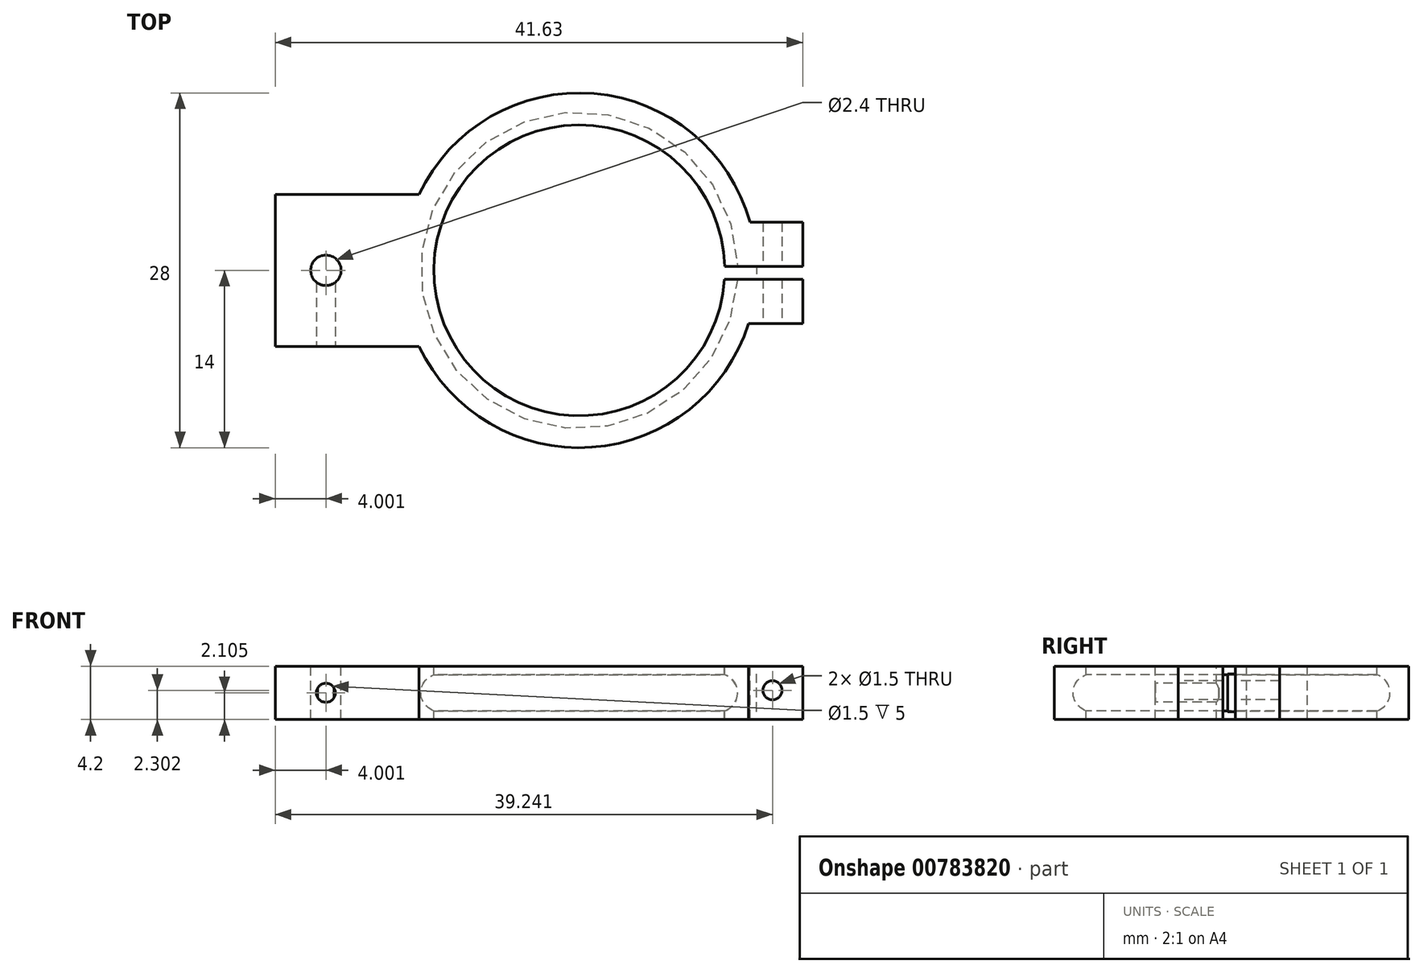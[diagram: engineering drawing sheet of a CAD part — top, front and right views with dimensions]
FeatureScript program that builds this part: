
annotation { "Feature Type Name" : "Feature", "Feature Type Description" : "" }
export const myFeature = defineFeature(function(context is Context, id is Id, definition is map)
    precondition{}
    {
        {
            var Q0;
            Q0=qCreatedBy(makeId("Front.planeOp"),FACE);
            var sketch = newSketch(context, id + "F0", { "sketchPlane" : qUnion([Q0])});
            skLineSegment(sketch, "E0", {"start": v(-17.32, 27.47) * mm, "end": v(-17.32, -17.12) * mm});
            skCircle(sketch, "E1", {"center": v(-28.32, 5.45) * mm, "radius": 1.5 * mm});
            skLineSegment(sketch, "E2", {"start": v(-28.32, 8.17) * mm, "end": v(-28.32, 2.71) * mm});
            skLineSegment(sketch, "E3", {"start": v(-28.32, 6.95) * mm, "end": v(-31.32, 6.95) * mm});
            skLineSegment(sketch, "E4", {"start": v(-28.32, 3.95) * mm, "end": v(-31.32, 3.95) * mm});
            skLineSegment(sketch, "E5", {"start": v(-31.32, 3.95) * mm, "end": v(-31.32, 6.95) * mm});
            skPoint(sketch, "E6.end.orphan", {"position": v(-28.32, 4.15) * mm});
            skPoint(sketch, "E6.start.orphan", {"position": v(-28.32, 6.75) * mm});
            skSolve(sketch);
        }
        {
            var Q0;
            {var subQ0=sQuery(id+"F0.wireOp",EDGE,"E3");Q0=makeQuery(id+"F0.imprint","IMPRINT",FACE,{"disambiguationData":[TD([[makeQuery(id+"F0.imprint","IMPRINT",EDGE,{"derivedFrom":subQ0}),1.0]])]});}
            var Q1;
            {var subQ0=sQuery(id+"F0.wireOp",EDGE,"4f6HL5Te-FB6r-DQlG-h35e-if1vYiqSxlt2");Q1=makeQuery(id+"F0.imprint","IMPRINT",FACE,{"disambiguationData":[TD([[makeQuery(id+"F0.imprint","IMPRINT",EDGE,{"derivedFrom":subQ0}),-1.0]])]});}
            var Q2;
            Q2=sQuery(id+"F0.wireOp",EDGE,"E0");
            revolve(context, id + "F1", {"surfaceOperationType" : NewSurfaceOperationType.NEW, "entities" : qUnion([Q0, Q1]), "axis" : qUnion([Q2]), "revolveType" : RevolveType.FULL});
        }
        {
            var Q0;
            Q0=makeQuery(id+"F1.opRevolve","SWEPT_FACE",FACE,{"disambiguationData":[OSD([sQuery(id+"F0.wireOp",EDGE,"E3")])]});
            var sketch = newSketch(context, id + "F2", { "sketchPlane" : qUnion([Q0])});
            skLineSegment(sketch, "E7.bottom", {"start": v(-4.13, 0.3) * mm, "end": v(-0.19, 0.3) * mm});
            skLineSegment(sketch, "E7.top", {"start": v(-4.13, 3.8) * mm, "end": v(-0.19, 3.8) * mm});
            skLineSegment(sketch, "E7.left", {"start": v(-4.13, 0.3) * mm, "end": v(-4.13, 3.8) * mm});
            skLineSegment(sketch, "E7.right", {"start": v(-0.19, 0.3) * mm, "end": v(-0.19, 3.8) * mm});
            skLineSegment(sketch, "E8.bottom", {"start": v(-4.13, -0.7) * mm, "end": v(-0.19, -0.7) * mm});
            skLineSegment(sketch, "E8.top", {"start": v(-4.13, -4.2) * mm, "end": v(-0.19, -4.2) * mm});
            skLineSegment(sketch, "E8.left", {"start": v(-4.13, -0.7) * mm, "end": v(-4.13, -4.2) * mm});
            skLineSegment(sketch, "E8.right", {"start": v(-0.19, -0.7) * mm, "end": v(-0.19, -4.2) * mm});
            skLineSegment(sketch, "E9.bottom", {"start": v(-29.4, 6) * mm, "end": v(-41.32, 6) * mm});
            skLineSegment(sketch, "E9.top", {"start": v(-29.4, -6) * mm, "end": v(-41.32, -6) * mm});
            skLineSegment(sketch, "E9.left", {"start": v(-29.4, 6) * mm, "end": v(-29.4, -6) * mm});
            skLineSegment(sketch, "E9.right", {"start": v(-41.32, 6) * mm, "end": v(-41.32, -6) * mm});
            skCircle(sketch, "E10", {"center": v(-37.32, 0) * mm, "radius": 1.2 * mm});
            skPoint(sketch, "E11", {"position": v(-17.32, 0) * mm});
            skSolve(sketch);
        }
        {
            var Q0;
            {var subQ0=sQuery(id+"F2.wireOp",EDGE,"E9.right");Q0=makeQuery(id+"F2.imprint","IMPRINT",FACE,{"disambiguationData":[TD([[makeQuery(id+"F2.imprint","IMPRINT",EDGE,{"derivedFrom":subQ0}),1.0]])]});}
            var Q1;
            {var subQ0=sQuery(id+"F2.wireOp",EDGE,"E7.right");Q1=makeQuery(id+"F2.imprint","IMPRINT",FACE,{"disambiguationData":[TD([[makeQuery(id+"F2.imprint","IMPRINT",EDGE,{"derivedFrom":subQ0}),1.0]])]});}
            var Q2;
            {var subQ0=sQuery(id+"F2.wireOp",EDGE,"E8.right");Q2=makeQuery(id+"F2.imprint","IMPRINT",FACE,{"disambiguationData":[TD([[makeQuery(id+"F2.imprint","IMPRINT",EDGE,{"derivedFrom":subQ0}),-1.0]])]});}
            extrude(context, id + "F3", {"entities" : qUnion([Q0, Q1, Q2]), "operationType" : NewBodyOperationType.ADD, "oppositeDirection" : true, "depth" : 3 * mm, "offsetDistance" : 25 * mm});
        }
        {
            var Q0;
            {var subQ0=sQuery(id+"F0.wireOp",EDGE,"E5");var subQ1=sQuery(id+"F0.wireOp",EDGE,"E3");Q0=makeQuery(id+"F3.boolean.opBoolean","MERGE",FACE,{"derivedFrom":[makeQuery(id+"F1.opRevolve","SWEPT_FACE",FACE,{"disambiguationData":[OSD([subQ1])]}),makeQuery(id+"F3.opExtrude","CAP_FACE",FACE,{"disambiguationData":[OSD([subQ1,subQ0,sQuery(id+"F2.wireOp",EDGE,"E7.bottom"),sQuery(id+"F2.wireOp",EDGE,"E7.top"),sQuery(id+"F2.wireOp",EDGE,"E7.right")])],"isStart":true}),makeQuery(id+"F3.opExtrude","CAP_FACE",FACE,{"disambiguationData":[OSD([subQ1,subQ0,sQuery(id+"F2.wireOp",EDGE,"E8.bottom"),sQuery(id+"F2.wireOp",EDGE,"E8.top"),sQuery(id+"F2.wireOp",EDGE,"E8.right")])],"isStart":true}),makeQuery(id+"F3.opExtrude","CAP_FACE",FACE,{"disambiguationData":[OSD([subQ1,subQ0,sQuery(id+"F2.wireOp",EDGE,"E9.bottom"),sQuery(id+"F2.wireOp",EDGE,"E9.top"),sQuery(id+"F2.wireOp",EDGE,"E9.right"),sQuery(id+"F2.wireOp",EDGE,"E10")])],"isStart":true})]});}
            var sketch = newSketch(context, id + "F4", { "sketchPlane" : qUnion([Q0])});
            skLineSegment(sketch, "E12.bottom", {"start": v(-3.32, 0.3) * mm, "end": v(-6.95, 0.3) * mm});
            skLineSegment(sketch, "E12.top", {"start": v(-3.32, -0.7) * mm, "end": v(-6.95, -0.7) * mm});
            skLineSegment(sketch, "E12.left", {"start": v(-3.32, 0.3) * mm, "end": v(-3.32, -0.7) * mm});
            skLineSegment(sketch, "E12.right", {"start": v(-6.95, 0.3) * mm, "end": v(-6.95, -0.7) * mm});
            skSolve(sketch);
        }
        {
            var Q0;
            {var subQ3=sQuery(id+"F0.wireOp",EDGE,"E3");var subQ9=makeQuery(id+"F1.opRevolve","SWEPT_EDGE",EDGE,{"disambiguationData":[OSD([sQuery(id+"F0.wireOp",EDGE,"E1"),sQuery(id+"F0.wireOp",EDGE,"E2"),sQuery(id+"F0.wireOp",EDGE,"4f6HL5Te-FB6r-DQlG-h35e-if1vYiqSxlt2"),subQ3])]});var subQ11=sQuery(id+"F4.wireOp",EDGE,"E12.bottom");var subQ13=makeQuery(id+"F4.imprint","INTERSECT",VERTEX,{"derivedFrom":[subQ9,subQ11]});Q0=makeQuery(id+"F4.imprint","IMPRINT",FACE,{"disambiguationData":[TD([[makeQuery(id+"F4.imprint","IMPRINT",EDGE,{"disambiguationData":[TD([[subQ13,1.0]])],"derivedFrom":subQ9}),-1.0]])]});}
            var Q1;
            {var subQ0=sQuery(id+"F4.wireOp",EDGE,"E12.right");Q1=makeQuery(id+"F4.imprint","IMPRINT",FACE,{"disambiguationData":[TD([[makeQuery(id+"F4.imprint","IMPRINT",EDGE,{"derivedFrom":subQ0}),1.0]])]});}
            extrude(context, id + "F5", {"entities" : qUnion([Q0, Q1]), "operationType" : NewBodyOperationType.REMOVE, "oppositeDirection" : true, "depth" : 25 * mm, "offsetDistance" : 25 * mm});
        }
        {
            var Q0;
            Q0=makeQuery(id+"F3.opExtrude","SWEPT_FACE",FACE,{"disambiguationData":[OSD([sQuery(id+"F2.wireOp",EDGE,"E8.top")])]});
            var sketch = newSketch(context, id + "F6", { "sketchPlane" : qUnion([Q0])});
            skCircle(sketch, "E13", {"center": v(-2.08, 5.65) * mm, "radius": 0.75 * mm});
            skSolve(sketch);
        }
        {
            var Q0;
            Q0 = qSketchRegion(id + "F6", true);
            extrude(context, id + "F7", {"entities" : qUnion([Q0]), "operationType" : NewBodyOperationType.REMOVE, "oppositeDirection" : true, "depth" : 25 * mm, "offsetDistance" : 25 * mm});
        }
        {
            var Q0;
            Q0=makeQuery(id+"F3.opExtrude","SWEPT_FACE",FACE,{"disambiguationData":[OSD([sQuery(id+"F2.wireOp",EDGE,"E9.top")])]});
            var sketch = newSketch(context, id + "F8", { "sketchPlane" : qUnion([Q0])});
            skCircle(sketch, "E14", {"center": v(-37.32, 5.45) * mm, "radius": 0.75 * mm});
            skPoint(sketch, "E14.centerSnap0", {"position": v(-41.32, 5.45) * mm});
            skSolve(sketch);
        }
        {
            var Q0;
            Q0=makeQuery(id+"F8.imprint","IMPRINT",FACE,{"disambiguationData":[TD([[makeQuery(id+"F8.imprint","IMPRINT",EDGE,{"derivedFrom":sQuery(id+"F8.wireOp",EDGE,"E14")}),1.0]])]});
            extrude(context, id + "F9", {"entities" : qUnion([Q0]), "operationType" : NewBodyOperationType.REMOVE, "oppositeDirection" : true, "depth" : 5 * mm, "offsetDistance" : 25 * mm});
        }
        {
            var Q0;
            {var subQ0=sQuery(id+"F0.wireOp",EDGE,"E5");var subQ1=sQuery(id+"F0.wireOp",EDGE,"E3");Q0=makeQuery(id+"F3.boolean.opBoolean","MERGE",FACE,{"derivedFrom":[makeQuery(id+"F1.opRevolve","SWEPT_FACE",FACE,{"disambiguationData":[OSD([subQ1])]}),makeQuery(id+"F3.opExtrude","CAP_FACE",FACE,{"disambiguationData":[OSD([subQ1,subQ0,sQuery(id+"F2.wireOp",EDGE,"E7.bottom"),sQuery(id+"F2.wireOp",EDGE,"E7.top"),sQuery(id+"F2.wireOp",EDGE,"E7.right")])],"isStart":true}),makeQuery(id+"F3.opExtrude","CAP_FACE",FACE,{"disambiguationData":[OSD([subQ1,subQ0,sQuery(id+"F2.wireOp",EDGE,"E8.bottom"),sQuery(id+"F2.wireOp",EDGE,"E8.top"),sQuery(id+"F2.wireOp",EDGE,"E8.right")])],"isStart":true}),makeQuery(id+"F3.opExtrude","CAP_FACE",FACE,{"disambiguationData":[OSD([subQ1,subQ0,sQuery(id+"F2.wireOp",EDGE,"E9.bottom"),sQuery(id+"F2.wireOp",EDGE,"E9.top"),sQuery(id+"F2.wireOp",EDGE,"E9.right"),sQuery(id+"F2.wireOp",EDGE,"E10")])],"isStart":true})]});}
            var sketch = newSketch(context, id + "F10", { "sketchPlane" : qUnion([Q0])});
            skSolve(sketch);
        }
        {
            var Q0;
            {var subQ7=sQuery(id+"F2.wireOp",EDGE,"E7.top");Q0=makeQuery(id+"F10.imprint","IMPRINT",FACE,{"disambiguationData":[TD([[makeQuery(id+"F10.imprint","IMPRINT",EDGE,{"derivedFrom":makeQuery(id+"F3.opExtrude","CAP_EDGE",EDGE,{"disambiguationData":[OSD([subQ7])],"isStart":true})}),-1.0]])]});}
            extrude(context, id + "F11", {"entities" : qUnion([Q0]), "operationType" : NewBodyOperationType.ADD, "depth" : 0.6 * mm, "offsetDistance" : 25 * mm});
        }
        {
            var Q0;
            {var subQ0=sQuery(id+"F0.wireOp",EDGE,"E5");var subQ1=sQuery(id+"F0.wireOp",EDGE,"E3");Q0=makeQuery(id+"F3.boolean.opBoolean","MERGE",FACE,{"derivedFrom":[makeQuery(id+"F1.opRevolve","SWEPT_FACE",FACE,{"disambiguationData":[OSD([sQuery(id+"F0.wireOp",EDGE,"E4")])]}),makeQuery(id+"F3.opExtrude","CAP_FACE",FACE,{"disambiguationData":[OSD([subQ1,subQ0,sQuery(id+"F2.wireOp",EDGE,"E7.bottom"),sQuery(id+"F2.wireOp",EDGE,"E7.top"),sQuery(id+"F2.wireOp",EDGE,"E7.right")])],"isStart":false}),makeQuery(id+"F3.opExtrude","CAP_FACE",FACE,{"disambiguationData":[OSD([subQ1,subQ0,sQuery(id+"F2.wireOp",EDGE,"E8.bottom"),sQuery(id+"F2.wireOp",EDGE,"E8.top"),sQuery(id+"F2.wireOp",EDGE,"E8.right")])],"isStart":false}),makeQuery(id+"F3.opExtrude","CAP_FACE",FACE,{"disambiguationData":[OSD([subQ1,subQ0,sQuery(id+"F2.wireOp",EDGE,"E9.bottom"),sQuery(id+"F2.wireOp",EDGE,"E9.top"),sQuery(id+"F2.wireOp",EDGE,"E9.right"),sQuery(id+"F2.wireOp",EDGE,"E10")])],"isStart":false})]});}
            var sketch = newSketch(context, id + "F12", { "sketchPlane" : qUnion([Q0])});
            skSolve(sketch);
        }
        {
            var Q0;
            {var subQ6=sQuery(id+"F2.wireOp",EDGE,"E7.top");Q0=makeQuery(id+"F12.imprint","IMPRINT",FACE,{"disambiguationData":[TD([[makeQuery(id+"F12.imprint","IMPRINT",EDGE,{"derivedFrom":makeQuery(id+"F3.opExtrude","CAP_EDGE",EDGE,{"disambiguationData":[OSD([subQ6])],"isStart":false})}),1.0]])]});}
            extrude(context, id + "F13", {"entities" : qUnion([Q0]), "operationType" : NewBodyOperationType.ADD, "depth" : 0.6 * mm, "offsetDistance" : 25 * mm});
        }
        {
            var Q0;
            {var subQ0=sQuery(id+"F2.wireOp",EDGE,"E7.right");Q0=makeQuery(id+"F13.boolean.opBoolean","MERGE",FACE,{"derivedFrom":[makeQuery(id+"F11.boolean.opBoolean","MERGE",FACE,{"derivedFrom":[makeQuery(id+"F3.opExtrude","SWEPT_FACE",FACE,{"disambiguationData":[OSD([subQ0])]}),makeQuery(id+"F11.opExtrude","SWEPT_FACE",FACE,{"disambiguationData":[OSD([subQ0])]})]}),makeQuery(id+"F13.opExtrude","SWEPT_FACE",FACE,{"disambiguationData":[OSD([subQ0])]})]});}
            var sketch = newSketch(context, id + "F14", { "sketchPlane" : qUnion([Q0])});
            skSolve(sketch);
        }
        {
            var Q0;
            {var subQ0=sQuery(id+"F2.wireOp",EDGE,"E7.right");Q0=makeQuery(id+"F14.imprint","IMPRINT",FACE,{"disambiguationData":[TD([[makeQuery(id+"F14.imprint","IMPRINT",EDGE,{"derivedFrom":makeQuery(id+"F11.opExtrude","CAP_EDGE",EDGE,{"disambiguationData":[OSD([subQ0])],"isStart":false})}),-1.0]])]});}
            var Q1;
            {var subQ0=sQuery(id+"F2.wireOp",EDGE,"E8.right");Q1=makeQuery(id+"F13.boolean.opBoolean","MERGE",FACE,{"derivedFrom":[makeQuery(id+"F11.boolean.opBoolean","MERGE",FACE,{"derivedFrom":[makeQuery(id+"F3.opExtrude","SWEPT_FACE",FACE,{"disambiguationData":[OSD([subQ0])]}),makeQuery(id+"F11.opExtrude","SWEPT_FACE",FACE,{"disambiguationData":[OSD([subQ0])]})]}),makeQuery(id+"F13.opExtrude","SWEPT_FACE",FACE,{"disambiguationData":[OSD([subQ0])]})]});}
            extrude(context, id + "F15", {"entities" : qUnion([Q0, Q1]), "operationType" : NewBodyOperationType.ADD, "depth" : 0.5 * mm, "offsetDistance" : 25 * mm});
        }
        {
            var Q0;
            {var subQ0=sQuery(id+"F2.wireOp",EDGE,"E7.right");var subQ1=sQuery(id+"F2.wireOp",EDGE,"E8.right");Q0=makeQuery(id+"F15.boolean.opBoolean","MERGE",FACE,{"derivedFrom":[makeQuery(id+"F11.opExtrude","CAP_FACE",FACE,{"disambiguationData":[OSD([sQuery(id+"F0.wireOp",EDGE,"E1"),sQuery(id+"F0.wireOp",EDGE,"E2"),sQuery(id+"F0.wireOp",EDGE,"E3"),sQuery(id+"F0.wireOp",EDGE,"E5"),sQuery(id+"F2.wireOp",EDGE,"E7.bottom"),sQuery(id+"F2.wireOp",EDGE,"E7.top"),subQ0,sQuery(id+"F2.wireOp",EDGE,"E8.bottom"),sQuery(id+"F2.wireOp",EDGE,"E8.top"),subQ1,sQuery(id+"F2.wireOp",EDGE,"E9.bottom"),sQuery(id+"F2.wireOp",EDGE,"E9.top"),sQuery(id+"F2.wireOp",EDGE,"E9.right"),sQuery(id+"F2.wireOp",EDGE,"E10"),sQuery(id+"F4.wireOp",EDGE,"E12.bottom"),sQuery(id+"F4.wireOp",EDGE,"E12.top")])],"isStart":false}),makeQuery(id+"F15.opExtrude","SWEPT_FACE",FACE,{"disambiguationData":[OSD([subQ1]),TDD([makeQuery(id+"F11.opExtrude","CAP_EDGE",EDGE,{"disambiguationData":[OSD([subQ1])],"isStart":false})])]}),makeQuery(id+"F15.opExtrude","SWEPT_FACE",FACE,{"disambiguationData":[OSD([subQ0]),TDD([makeQuery(id+"F14.imprint","IMPRINT",EDGE,{"derivedFrom":makeQuery(id+"F11.opExtrude","CAP_EDGE",EDGE,{"disambiguationData":[OSD([subQ0])],"isStart":false})})])]})]});}
            var sketch = newSketch(context, id + "F16", { "sketchPlane" : qUnion([Q0])});
            skCircle(sketch, "E15", {"center": v(-17.32, 0) * mm, "radius": 11.48 * mm});
            skSolve(sketch);
        }
        {
            var Q0;
            {var subQ14=sQuery(id+"F0.wireOp",EDGE,"E3");var subQ20=makeQuery(id+"F11.opExtrude","CAP_EDGE",EDGE,{"disambiguationData":[OSD([sQuery(id+"F0.wireOp",EDGE,"E1"),sQuery(id+"F0.wireOp",EDGE,"E2"),subQ14])],"isStart":false});Q0=makeQuery(id+"F16.imprint","IMPRINT",FACE,{"disambiguationData":[TD([[makeQuery(id+"F16.imprint","IMPRINT",EDGE,{"derivedFrom":subQ20}),-1.0]])]});}
            extrude(context, id + "F17", {"entities" : qUnion([Q0]), "operationType" : NewBodyOperationType.REMOVE, "oppositeDirection" : true, "depth" : 25 * mm, "offsetDistance" : 25 * mm});
        }
    });
